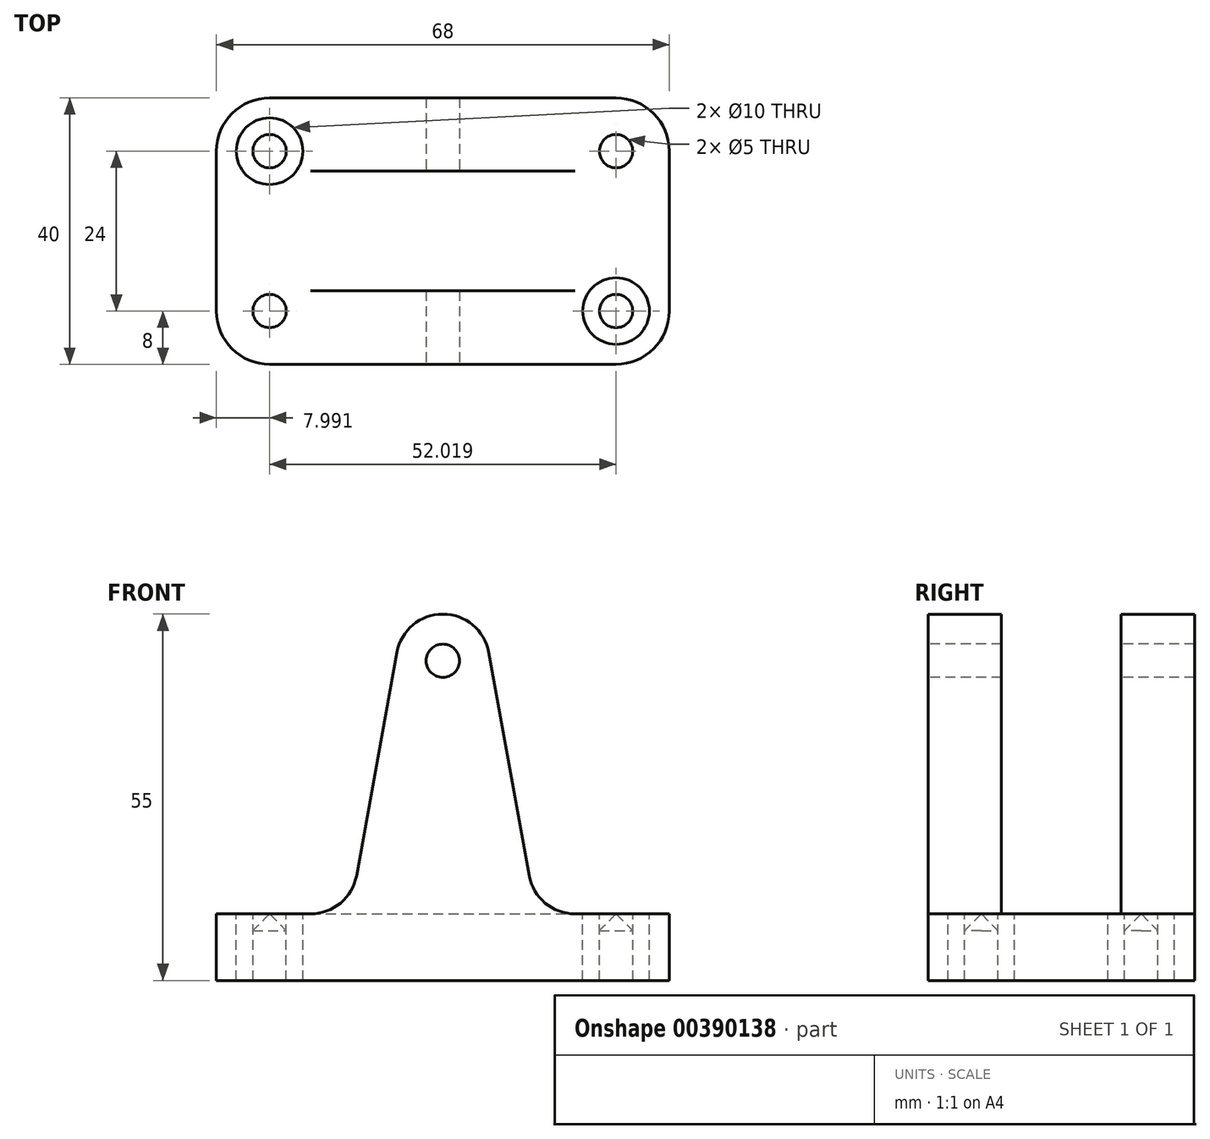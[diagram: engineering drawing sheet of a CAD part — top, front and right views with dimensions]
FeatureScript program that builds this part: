
annotation { "Feature Type Name" : "Feature", "Feature Type Description" : "" }
export const myFeature = defineFeature(function(context is Context, id is Id, definition is map)
    precondition{}
    {
        {
            var Q0;
            Q0=qCreatedBy(makeId("Front.planeOp"),FACE);
            var sketch = newSketch(context, id + "F0", { "sketchPlane" : qUnion([Q0])});
            skLineSegment(sketch, "E0", {"start": v(0, -39.8) * mm, "end": v(-34, -39.8) * mm});
            skLineSegment(sketch, "E1", {"start": v(0, -39.8) * mm, "end": v(34, -39.8) * mm});
            skLineSegment(sketch, "E2", {"start": v(34, -39.8) * mm, "end": v(34, -29.8) * mm});
            skLineSegment(sketch, "E3.MirrorCS", {"start": v(-34, -39.8) * mm, "end": v(-34, -29.8) * mm});
            skLineSegment(sketch, "E4", {"start": v(-34, -29.8) * mm, "end": v(34, -29.8) * mm});
            skLineSegment(sketch, "E5", {"start": v(0, -39.8) * mm, "end": v(0, 8.2) * mm, "construction": true});
            skCircle(sketch, "E6", {"center": v(0, 8.2) * mm, "radius": 2.5 * mm});
            skArc(sketch, "E7", {"start": v(6.89, 9.45) * mm, "mid": v(0, 15.2) * mm, "end": v(-6.89, 9.45) * mm});
            skLineSegment(sketch, "E8", {"start": v(14, -29.8) * mm, "end": v(6.89, 9.45) * mm});
            skLineSegment(sketch, "E9", {"start": v(-14, -29.8) * mm, "end": v(-6.89, 9.45) * mm});
            skSolve(sketch);
        }
        {
            var Q0;
            Q0=makeQuery(id+"F0.imprint","IMPRINT",FACE,{"disambiguationData":[TD([[makeQuery(id+"F0.imprint","IMPRINT",EDGE,{"derivedFrom":sQuery(id+"F0.wireOp",EDGE,"E6")}),-1.0]])]});
            var Q1;
            Q1=makeQuery(id+"F0.imprint","IMPRINT",FACE,{"disambiguationData":[TD([[makeQuery(id+"F0.imprint","IMPRINT",EDGE,{"derivedFrom":sQuery(id+"F0.wireOp",EDGE,"E0")}),-1.0]])]});
            extrude(context, id + "F1", {"entities" : qUnion([Q0, Q1]), "oppositeDirection" : true, "depth" : 40 * mm});
        }
        {
            var Q0;
            {var subQ0=sQuery(id+"F0.wireOp",EDGE,"E4");Q0=makeQuery(id+"F1.opExtrude","SWEPT_FACE",FACE,{"disambiguationData":[OSD([subQ0]),TDD([makeQuery(id+"F0.imprint","IMPRINT",EDGE,{"disambiguationData":[TD([[makeQuery(id+"F0.imprint","INTERSECT",VERTEX,{"derivedFrom":[sQuery(id+"F0.wireOp",EDGE,"E3.MirrorCS"),subQ0]}),-1.0]])],"derivedFrom":subQ0})])]});}
            var sketch = newSketch(context, id + "F2", { "sketchPlane" : qUnion([Q0])});
            skCircle(sketch, "E10.MirrorC", {"center": v(26, 32) * mm, "radius": 2.5 * mm});
            skCircle(sketch, "E11.MirrorC", {"center": v(26, 32) * mm, "radius": 5 * mm});
            skCircle(sketch, "E12.MirrorC", {"center": v(-26, 32) * mm, "radius": 2.5 * mm});
            skCircle(sketch, "E13.MirrorC", {"center": v(-26, 32) * mm, "radius": 5 * mm});
            skCircle(sketch, "E14.MirrorC", {"center": v(-26, 8) * mm, "radius": 2.5 * mm});
            skCircle(sketch, "E15.MirrorC", {"center": v(-26, 8) * mm, "radius": 5 * mm});
            skCircle(sketch, "E16.MirrorC", {"center": v(26, 8) * mm, "radius": 2.5 * mm});
            skCircle(sketch, "E17.MirrorC", {"center": v(26, 8) * mm, "radius": 5 * mm});
            skLineSegment(sketch, "E18", {"start": v(-26, 37) * mm, "end": v(-26, 27) * mm, "construction": true});
            skLineSegment(sketch, "E19", {"start": v(-26, 13) * mm, "end": v(-26, 3) * mm, "construction": true});
            skLineSegment(sketch, "E20", {"start": v(26, 37) * mm, "end": v(26, 27) * mm, "construction": true});
            skLineSegment(sketch, "E21", {"start": v(26, 13) * mm, "end": v(26, 3) * mm, "construction": true});
            skLineSegment(sketch, "E22", {"start": v(31, 8) * mm, "end": v(21, 8) * mm, "construction": true});
            skLineSegment(sketch, "E23", {"start": v(31, 32) * mm, "end": v(21, 32) * mm, "construction": true});
            skLineSegment(sketch, "E24", {"start": v(-31, 8) * mm, "end": v(-21, 8) * mm, "construction": true});
            skLineSegment(sketch, "E25", {"start": v(-31, 32) * mm, "end": v(-21, 32) * mm, "construction": true});
            skSolve(sketch);
        }
        {
            var Q0;
            Q0=qSketchRegion(id+"F2",true);
            extrude(context, id + "F3", {"entities" : qUnion([Q0]), "operationType" : NewBodyOperationType.REMOVE, "oppositeDirection" : true, "depth" : 3 * mm});
        }
        {
            var Q0;
            {var subQ1=sQuery(id+"F0.wireOp",EDGE,"E3.MirrorCS");var subQ5=sQuery(id+"F0.wireOp",EDGE,"E4");Q0=makeQuery(id+"F3.boolean.opBoolean","SPLIT",FACE,{"disambiguationData":[TD([makeQuery(id+"F1.opExtrude","SWEPT_FACE",FACE,{"disambiguationData":[OSD([subQ1])]})])],"derivedFrom":makeQuery(id+"F1.opExtrude","SWEPT_FACE",FACE,{"disambiguationData":[OSD([subQ5]),TDD([makeQuery(id+"F0.imprint","IMPRINT",EDGE,{"disambiguationData":[TD([[makeQuery(id+"F0.imprint","INTERSECT",VERTEX,{"derivedFrom":[subQ1,subQ5]}),-1.0]])],"derivedFrom":subQ5})])]})});}
            var sketch = newSketch(context, id + "F4", { "sketchPlane" : qUnion([Q0])});
            skLineSegment(sketch, "E26", {"start": v(-34, 0) * mm, "end": v(-34, 20) * mm, "construction": true});
            skLineSegment(sketch, "E27", {"start": v(-34, 20) * mm, "end": v(0, 20) * mm, "construction": true});
            skLineSegment(sketch, "E28", {"start": v(0, 20) * mm, "end": v(0, 32) * mm, "construction": true});
            skLineSegment(sketch, "E29", {"start": v(0, 20) * mm, "end": v(0, 8) * mm, "construction": true});
            skLineSegment(sketch, "E30", {"start": v(-18.64, 28.99) * mm, "end": v(18.64, 28.99) * mm});
            skLineSegment(sketch, "E31.MirrorCS", {"start": v(-18.64, 11.01) * mm, "end": v(18.64, 11.01) * mm});
            skLineSegment(sketch, "E32", {"start": v(18.64, 28.99) * mm, "end": v(18.64, 11.01) * mm});
            skLineSegment(sketch, "E33.MirrorCS", {"start": v(-18.64, 28.99) * mm, "end": v(-18.64, 11.01) * mm});
            skPoint(sketch, "E34.orphan", {"position": v(30, 28.99) * mm});
            skPoint(sketch, "E35.orphan", {"position": v(30, 11.01) * mm});
            skPoint(sketch, "E36.orphan", {"position": v(-30, 28.99) * mm});
            skPoint(sketch, "E37.orphan", {"position": v(-30, 11.01) * mm});
            skSolve(sketch);
        }
        {
            var Q0;
            {var subQ0=sQuery(id+"F4.wireOp",EDGE,"f66d0ab9-449e-4d87-a520-3055bb65471c0.MirrorCS");var subQ1=sQuery(id+"F4.wireOp",EDGE,"E30");var subQ2=makeQuery(id+"F4.imprint","INTERSECT",VERTEX,{"derivedFrom":[subQ1,subQ0]});Q0=makeQuery(id+"F4.imprint","IMPRINT",FACE,{"disambiguationData":[TD([[makeQuery(id+"F4.imprint","IMPRINT",EDGE,{"disambiguationData":[TD([[subQ2,1.0]])],"derivedFrom":subQ0}),1.0]])]});}
            var Q1;
            {var subQ0=sQuery(id+"F4.wireOp",EDGE,"E30");var subQ6=makeQuery(id+"F3.boolean.opBoolean","COPY",EDGE,{"derivedFrom":makeQuery(id+"F3.opExtrude","CAP_EDGE",EDGE,{"disambiguationData":[OSD([sQuery(id+"F2.wireOp",EDGE,"E13.MirrorC")])],"isStart":true})});var subQ11=makeQuery(id+"F4.imprint","INTERSECT",VERTEX,{"derivedFrom":[subQ6,subQ0]});Q1=makeQuery(id+"F4.imprint","IMPRINT",FACE,{"disambiguationData":[TD([[makeQuery(id+"F4.imprint","IMPRINT",EDGE,{"disambiguationData":[TD([[subQ11,-1.0]])],"derivedFrom":subQ0}),-1.0]])]});}
            extrude(context, id + "F5", {"entities" : qUnion([Q0, Q1]), "operationType" : NewBodyOperationType.REMOVE, "depth" : 50 * mm});
        }
        {
            var Q0;
            Q0=makeQuery(id+"F1.opExtrude","CAP_EDGE",EDGE,{"disambiguationData":[OSD([sQuery(id+"F0.wireOp",EDGE,"E3.MirrorCS")])],"isStart":true});
            var Q1;
            Q1=makeQuery(id+"F1.opExtrude","CAP_EDGE",EDGE,{"disambiguationData":[OSD([sQuery(id+"F0.wireOp",EDGE,"E2")])],"isStart":true});
            var Q2;
            Q2=makeQuery(id+"F1.opExtrude","CAP_EDGE",EDGE,{"disambiguationData":[OSD([sQuery(id+"F0.wireOp",EDGE,"E2")])],"isStart":false});
            var Q3;
            Q3=makeQuery(id+"F1.opExtrude","CAP_EDGE",EDGE,{"disambiguationData":[OSD([sQuery(id+"F0.wireOp",EDGE,"E3.MirrorCS")])],"isStart":false});
            fillet(context, id + "F6", {"entities" : qUnion([Q0, Q1, Q2, Q3]), "radius" : 8 * mm, "tangentPropagation" : true, "allowEdgeOverflow" : false});
        }
        {
            var Q0;
            Q0=makeQuery(id+"F3.boolean.opBoolean","COPY",FACE,{"derivedFrom":makeQuery(id+"F3.opExtrude","CAP_FACE",FACE,{"disambiguationData":[OSD([sQuery(id+"F2.wireOp",EDGE,"E12.MirrorC"),sQuery(id+"F2.wireOp",EDGE,"E13.MirrorC")])],"isStart":false})});
            var sketch = newSketch(context, id + "F7", { "sketchPlane" : qUnion([Q0])});
            skCircle(sketch, "E38", {"center": v(-26, 32) * mm, "radius": 2.5 * mm});
            skCircle(sketch, "E39", {"center": v(-26, 32) * mm, "radius": 5 * mm});
            skCircle(sketch, "E40.MirrorC", {"center": v(26, 32) * mm, "radius": 2.5 * mm});
            skCircle(sketch, "E41.MirrorC", {"center": v(26, 32) * mm, "radius": 5 * mm});
            skCircle(sketch, "E42.MirrorC", {"center": v(26, 8) * mm, "radius": 2.5 * mm});
            skCircle(sketch, "E43.MirrorC", {"center": v(26, 8) * mm, "radius": 5 * mm});
            skCircle(sketch, "E44.MirrorC", {"center": v(-26, 8) * mm, "radius": 2.5 * mm});
            skCircle(sketch, "E45.MirrorC", {"center": v(-26, 8) * mm, "radius": 5 * mm});
            skSolve(sketch);
        }
        {
            var Q0;
            Q0=makeQuery(id+"F0.imprint","IMPRINT",FACE,{"disambiguationData":[TD([[makeQuery(id+"F0.imprint","IMPRINT",EDGE,{"derivedFrom":sQuery(id+"F0.wireOp",EDGE,"E0")}),-1.0]])]});
            cPlane(context, id + "F8", {"entities" : qUnion([Q0]), "cplaneType" : CPlaneType.OFFSET, "offset" : 8 * mm, "oppositeDirection" : true, "width" : 150 * mm, "height" : 150 * mm});
        }
        {
            var Q0;
            {var subQ0=sQuery(id+"F0.wireOp",EDGE,"E9");var subQ1=sQuery(id+"F0.wireOp",EDGE,"E4");var subQ5=sQuery(id+"F4.wireOp",EDGE,"E31.MirrorCS");Q0=makeQuery(id+"F5.boolean.opBoolean","SPLIT",EDGE,{"disambiguationData":[TD([makeQuery(id+"F5.opExtrude","SWEPT_FACE",FACE,{"disambiguationData":[OSD([subQ5])]})])],"derivedFrom":makeQuery(id+"F1.opExtrude","SWEPT_EDGE",EDGE,{"disambiguationData":[OSD([subQ1,subQ0])]})});}
            var Q1;
            {var subQ0=sQuery(id+"F0.wireOp",EDGE,"E4");var subQ3=sQuery(id+"F0.wireOp",EDGE,"E9");var subQ5=sQuery(id+"F4.wireOp",EDGE,"E30");Q1=makeQuery(id+"F5.boolean.opBoolean","SPLIT",EDGE,{"disambiguationData":[TD([makeQuery(id+"F5.opExtrude","SWEPT_FACE",FACE,{"disambiguationData":[OSD([subQ5])]})])],"derivedFrom":makeQuery(id+"F1.opExtrude","SWEPT_EDGE",EDGE,{"disambiguationData":[OSD([subQ0,subQ3])]})});}
            var Q2;
            {var subQ0=sQuery(id+"F0.wireOp",EDGE,"E8");var subQ1=sQuery(id+"F0.wireOp",EDGE,"E4");var subQ5=sQuery(id+"F4.wireOp",EDGE,"E31.MirrorCS");Q2=makeQuery(id+"F5.boolean.opBoolean","SPLIT",EDGE,{"disambiguationData":[TD([makeQuery(id+"F5.opExtrude","SWEPT_FACE",FACE,{"disambiguationData":[OSD([subQ5])]})])],"derivedFrom":makeQuery(id+"F1.opExtrude","SWEPT_EDGE",EDGE,{"disambiguationData":[OSD([subQ1,subQ0])]})});}
            var Q3;
            {var subQ0=sQuery(id+"F0.wireOp",EDGE,"E8");var subQ1=sQuery(id+"F0.wireOp",EDGE,"E4");var subQ5=sQuery(id+"F4.wireOp",EDGE,"E30");Q3=makeQuery(id+"F5.boolean.opBoolean","SPLIT",EDGE,{"disambiguationData":[TD([makeQuery(id+"F5.opExtrude","SWEPT_FACE",FACE,{"disambiguationData":[OSD([subQ5])]})])],"derivedFrom":makeQuery(id+"F1.opExtrude","SWEPT_EDGE",EDGE,{"disambiguationData":[OSD([subQ1,subQ0])]})});}
            fillet(context, id + "F9", {"entities" : qUnion([Q0, Q1, Q2, Q3]), "radius" : 7 * mm, "tangentPropagation" : true, "allowEdgeOverflow" : false});
        }
        {
            var Q0;
            Q0=qSketchRegion(id+"F7",true);
            extrude(context, id + "F10", {"entities" : qUnion([Q0]), "operationType" : NewBodyOperationType.ADD, "depth" : 3 * mm});
        }
        {
            var Q0;
            Q0=makeQuery(id+"F2.imprint","IMPRINT",FACE,{"disambiguationData":[TD([[makeQuery(id+"F2.imprint","IMPRINT",EDGE,{"derivedFrom":sQuery(id+"F2.wireOp",EDGE,"E12.MirrorC")}),-1.0]])]});
            var Q1;
            Q1=makeQuery(id+"F2.imprint","IMPRINT",FACE,{"disambiguationData":[TD([[makeQuery(id+"F2.imprint","IMPRINT",EDGE,{"derivedFrom":sQuery(id+"F2.wireOp",EDGE,"E14.MirrorC")}),1.0]])]});
            var Q2;
            Q2=makeQuery(id+"F2.imprint","IMPRINT",FACE,{"disambiguationData":[TD([[makeQuery(id+"F2.imprint","IMPRINT",EDGE,{"derivedFrom":sQuery(id+"F2.wireOp",EDGE,"E16.MirrorC")}),-1.0]])]});
            var Q3;
            Q3=makeQuery(id+"F2.imprint","IMPRINT",FACE,{"disambiguationData":[TD([[makeQuery(id+"F2.imprint","IMPRINT",EDGE,{"derivedFrom":sQuery(id+"F2.wireOp",EDGE,"E10.MirrorC")}),1.0]])]});
            extrude(context, id + "F11", {"entities" : qUnion([Q0, Q1, Q2, Q3]), "operationType" : NewBodyOperationType.REMOVE, "oppositeDirection" : true, "depth" : 25 * mm});
        }
        {
            var Q0;
            Q0=makeQuery(id+"F11.boolean.opBoolean","COPY",EDGE,{"derivedFrom":makeQuery(id+"F11.opExtrude","CAP_EDGE",EDGE,{"disambiguationData":[OSD([sQuery(id+"F2.wireOp",EDGE,"E12.MirrorC")])],"isStart":true})});
            var Q1;
            Q1=makeQuery(id+"F11.boolean.opBoolean","COPY",EDGE,{"derivedFrom":makeQuery(id+"F11.opExtrude","CAP_EDGE",EDGE,{"disambiguationData":[OSD([sQuery(id+"F2.wireOp",EDGE,"E10.MirrorC")])],"isStart":true})});
            var Q2;
            Q2=makeQuery(id+"F11.boolean.opBoolean","COPY",EDGE,{"derivedFrom":makeQuery(id+"F11.opExtrude","CAP_EDGE",EDGE,{"disambiguationData":[OSD([sQuery(id+"F2.wireOp",EDGE,"E16.MirrorC")])],"isStart":true})});
            var Q3;
            Q3=makeQuery(id+"F11.boolean.opBoolean","COPY",EDGE,{"derivedFrom":makeQuery(id+"F11.opExtrude","CAP_EDGE",EDGE,{"disambiguationData":[OSD([sQuery(id+"F2.wireOp",EDGE,"E14.MirrorC")])],"isStart":true})});
            chamfer(context, id + "F12", {"entities" : qUnion([Q0, Q1, Q2, Q3]), "chamferType" : ChamferType.OFFSET_ANGLE, "width" : 2.5 * mm, "oppositeDirection" : false, "angle" : 45 * degree, "tangentPropagation" : true});
        }
    });
